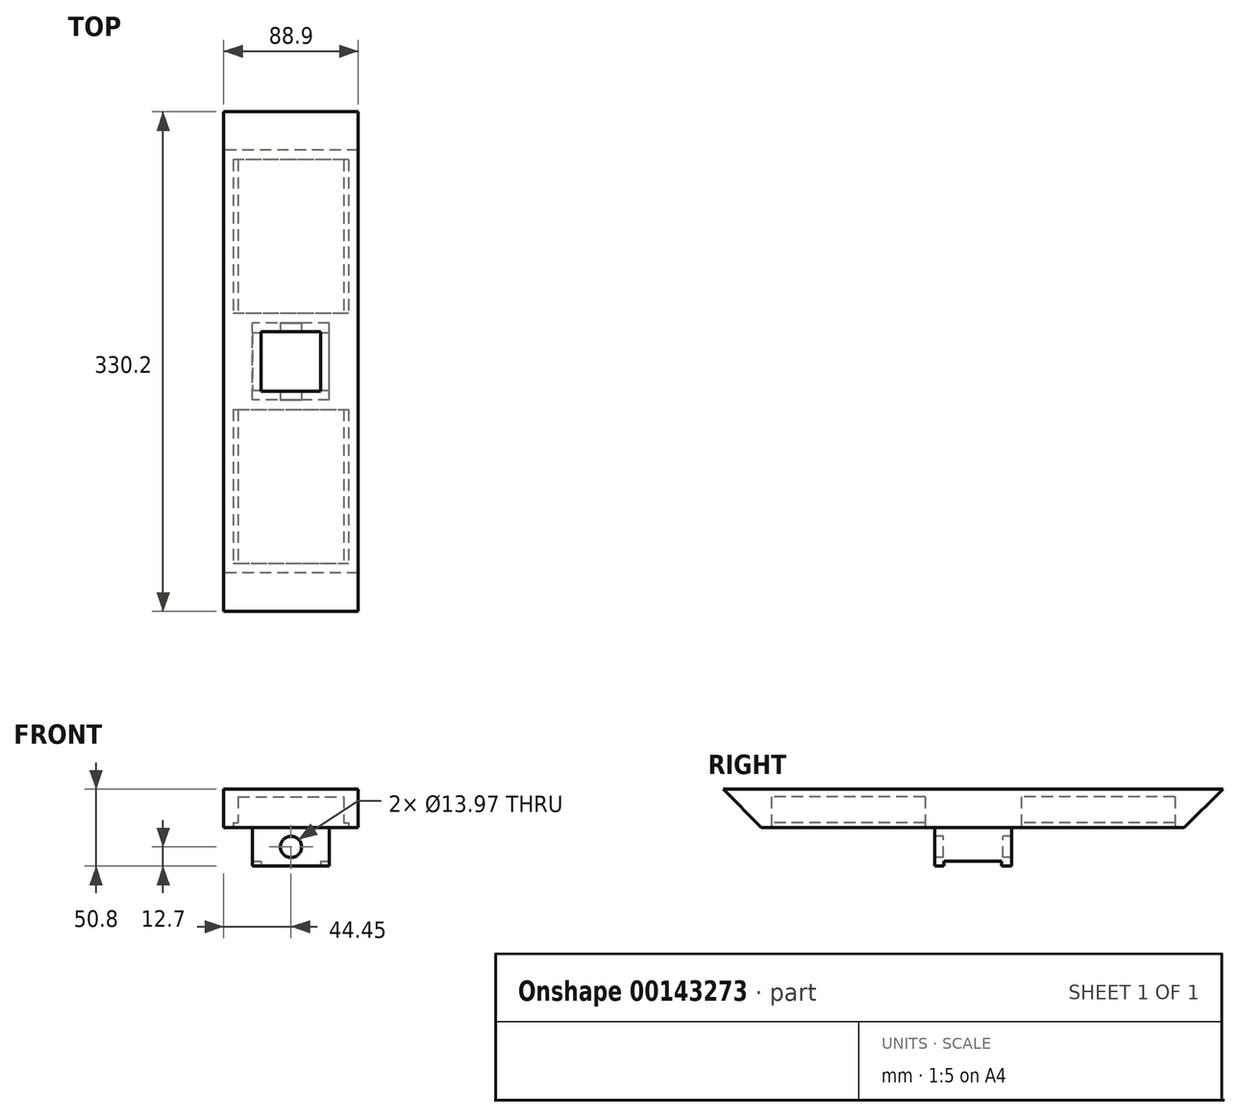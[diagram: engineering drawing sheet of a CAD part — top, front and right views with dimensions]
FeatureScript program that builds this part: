
annotation { "Feature Type Name" : "Feature", "Feature Type Description" : "" }
export const myFeature = defineFeature(function(context is Context, id is Id, definition is map)
    precondition{}
    {
        {
            var Q0;
            Q0=qCreatedBy(makeId("Top.planeOp"),FACE);
            var sketch = newSketch(context, id + "F0", { "sketchPlane" : qUnion([Q0])});
            skLineSegment(sketch, "E0.bottom", {"start": v(25.4, -25.4) * mm, "end": v(-25.4, -25.4) * mm});
            skLineSegment(sketch, "E0.top", {"start": v(25.4, 25.4) * mm, "end": v(-25.4, 25.4) * mm});
            skLineSegment(sketch, "E0.left", {"start": v(25.4, -25.4) * mm, "end": v(25.4, 25.4) * mm});
            skLineSegment(sketch, "E0.right", {"start": v(-25.4, -25.4) * mm, "end": v(-25.4, 25.4) * mm});
            skPoint(sketch, "E0.middle", {"position": v(0, 0) * mm});
            skLineSegment(sketch, "E1.bottom", {"start": v(19.69, -19.69) * mm, "end": v(-19.68, -19.69) * mm});
            skLineSegment(sketch, "E1.top", {"start": v(19.69, 19.69) * mm, "end": v(-19.69, 19.68) * mm});
            skLineSegment(sketch, "E1.left", {"start": v(19.69, -19.69) * mm, "end": v(19.69, 19.69) * mm});
            skLineSegment(sketch, "E1.right", {"start": v(-19.68, -19.69) * mm, "end": v(-19.68, 19.69) * mm});
            skSolve(sketch);
        }
        {
            var Q0;
            Q0 = qSketchRegion(id + "F0", true);
            extrude(context, id + "F1", {"entities" : qUnion([Q0]), "depth" : 25.4 * mm});
        }
        {
            var Q0;
            Q0=makeQuery(id+"F1.opExtrude","SWEPT_FACE",FACE,{"disambiguationData":[OSD([sQuery(id+"F0.wireOp",EDGE,"E0.bottom")])]});
            var sketch = newSketch(context, id + "F2", { "sketchPlane" : qUnion([Q0])});
            skCircle(sketch, "E2", {"center": v(0, 12.7) * mm, "radius": 6.99 * mm});
            skPoint(sketch, "E2.centerSnap0", {"position": v(-25.4, 12.7) * mm});
            skSolve(sketch);
        }
        {
            var Q0;
            Q0 = qSketchRegion(id + "F2", true);
            extrude(context, id + "F3", {"entities" : qUnion([Q0]), "operationType" : NewBodyOperationType.REMOVE, "endBound" : BoundingType.THROUGH_ALL, "oppositeDirection" : true, "depth" : 25.4 * mm});
        }
        {
            var Q0;
            Q0=makeQuery(id+"F1.opExtrude","CAP_FACE",FACE,{"disambiguationData":[OSD([sQuery(id+"F0.wireOp",EDGE,"E0.bottom"),sQuery(id+"F0.wireOp",EDGE,"E0.top"),sQuery(id+"F0.wireOp",EDGE,"E0.left"),sQuery(id+"F0.wireOp",EDGE,"E0.right"),sQuery(id+"F0.wireOp",EDGE,"E1.bottom"),sQuery(id+"F0.wireOp",EDGE,"E1.top"),sQuery(id+"F0.wireOp",EDGE,"E1.left"),sQuery(id+"F0.wireOp",EDGE,"E1.right")])],"isStart":false});
            var sketch = newSketch(context, id + "F4", { "sketchPlane" : qUnion([Q0])});
            skLineSegment(sketch, "E3.bottom", {"start": v(44.45, -139.7) * mm, "end": v(-44.45, -139.7) * mm});
            skLineSegment(sketch, "E3.top", {"start": v(44.45, 139.7) * mm, "end": v(-44.45, 139.7) * mm});
            skLineSegment(sketch, "E3.left", {"start": v(44.45, -139.7) * mm, "end": v(44.45, 139.7) * mm});
            skLineSegment(sketch, "E3.right", {"start": v(-44.45, -139.7) * mm, "end": v(-44.45, 139.7) * mm});
            skPoint(sketch, "E3.middle", {"position": v(0, 0) * mm});
            skLineSegment(sketch, "E4.bottom", {"start": v(19.69, 19.69) * mm, "end": v(-19.69, 19.69) * mm});
            skLineSegment(sketch, "E4.top", {"start": v(19.69, -19.69) * mm, "end": v(-19.69, -19.69) * mm});
            skLineSegment(sketch, "E4.left", {"start": v(19.69, 19.69) * mm, "end": v(19.69, -19.69) * mm});
            skLineSegment(sketch, "E4.right", {"start": v(-19.69, 19.69) * mm, "end": v(-19.69, -19.69) * mm});
            skSolve(sketch);
        }
        {
            var Q0;
            Q0 = qSketchRegion(id + "F4", true);
            extrude(context, id + "F5", {"entities" : qUnion([Q0]), "operationType" : NewBodyOperationType.ADD, "depth" : 25.4 * mm});
        }
        {
            var Q0;
            Q0=makeQuery(id+"F5.opExtrude","CAP_FACE",FACE,{"disambiguationData":[OSD([sQuery(id+"F4.wireOp",EDGE,"E3.bottom"),sQuery(id+"F4.wireOp",EDGE,"E3.top"),sQuery(id+"F4.wireOp",EDGE,"E3.left"),sQuery(id+"F4.wireOp",EDGE,"E3.right"),sQuery(id+"F4.wireOp",EDGE,"E4.bottom"),sQuery(id+"F4.wireOp",EDGE,"E4.top"),sQuery(id+"F4.wireOp",EDGE,"E4.left"),sQuery(id+"F4.wireOp",EDGE,"E4.right")])],"isStart":true});
            var sketch = newSketch(context, id + "F6", { "sketchPlane" : qUnion([Q0])});
            skLineSegment(sketch, "E5.bottom", {"start": v(44.45, 139.7) * mm, "end": v(38.1, 139.7) * mm});
            skLineSegment(sketch, "E5.top", {"start": v(44.45, 133.35) * mm, "end": v(38.1, 133.35) * mm});
            skLineSegment(sketch, "E5.left", {"start": v(44.45, 139.7) * mm, "end": v(44.45, 133.35) * mm});
            skLineSegment(sketch, "E5.right", {"start": v(38.1, 139.7) * mm, "end": v(38.1, 133.35) * mm});
            skLineSegment(sketch, "E6.bottom", {"start": v(-44.45, 25.4) * mm, "end": v(-38.1, 25.4) * mm});
            skLineSegment(sketch, "E6.top", {"start": v(-44.45, 31.75) * mm, "end": v(-38.1, 31.75) * mm});
            skLineSegment(sketch, "E6.left", {"start": v(-44.45, 25.4) * mm, "end": v(-44.45, 31.75) * mm});
            skLineSegment(sketch, "E6.right", {"start": v(-38.1, 25.4) * mm, "end": v(-38.1, 31.75) * mm});
            skLineSegment(sketch, "E7.bottom", {"start": v(-44.45, -25.4) * mm, "end": v(-38.1, -25.4) * mm});
            skLineSegment(sketch, "E7.top", {"start": v(-44.45, -31.75) * mm, "end": v(-38.1, -31.75) * mm});
            skLineSegment(sketch, "E7.left", {"start": v(-44.45, -25.4) * mm, "end": v(-44.45, -31.75) * mm});
            skLineSegment(sketch, "E7.right", {"start": v(-38.1, -25.4) * mm, "end": v(-38.1, -31.75) * mm});
            skLineSegment(sketch, "E8.bottom", {"start": v(44.45, -139.7) * mm, "end": v(38.1, -139.7) * mm});
            skLineSegment(sketch, "E8.top", {"start": v(44.45, -133.35) * mm, "end": v(38.1, -133.35) * mm});
            skLineSegment(sketch, "E8.left", {"start": v(44.45, -139.7) * mm, "end": v(44.45, -133.35) * mm});
            skLineSegment(sketch, "E8.right", {"start": v(38.1, -139.7) * mm, "end": v(38.1, -133.35) * mm});
            skLineSegment(sketch, "E9.bottom", {"start": v(38.1, -133.35) * mm, "end": v(-38.1, -133.35) * mm});
            skLineSegment(sketch, "E9.top", {"start": v(38.1, -31.75) * mm, "end": v(-38.1, -31.75) * mm});
            skLineSegment(sketch, "E9.left", {"start": v(38.1, -133.35) * mm, "end": v(38.1, -31.75) * mm});
            skLineSegment(sketch, "E9.right", {"start": v(-38.1, -133.35) * mm, "end": v(-38.1, -31.75) * mm});
            skLineSegment(sketch, "E10.bottom", {"start": v(-38.1, 31.75) * mm, "end": v(38.1, 31.75) * mm});
            skLineSegment(sketch, "E10.top", {"start": v(-38.1, 133.35) * mm, "end": v(38.1, 133.35) * mm});
            skLineSegment(sketch, "E10.left", {"start": v(-38.1, 31.75) * mm, "end": v(-38.1, 133.35) * mm});
            skLineSegment(sketch, "E10.right", {"start": v(38.1, 31.75) * mm, "end": v(38.1, 133.35) * mm});
            skSolve(sketch);
        }
        {
            var Q0;
            Q0=makeQuery(id+"F6.imprint","IMPRINT",FACE,{"disambiguationData":[TD([[makeQuery(id+"F6.imprint","IMPRINT",EDGE,{"derivedFrom":sQuery(id+"F6.wireOp",EDGE,"E9.bottom")}),-1.0]])]});
            var Q1;
            Q1=makeQuery(id+"F6.imprint","IMPRINT",FACE,{"disambiguationData":[TD([[makeQuery(id+"F6.imprint","IMPRINT",EDGE,{"derivedFrom":sQuery(id+"F6.wireOp",EDGE,"E10.bottom")}),1.0]])]});
            extrude(context, id + "F7", {"entities" : qUnion([Q0, Q1]), "operationType" : NewBodyOperationType.REMOVE, "oppositeDirection" : true, "depth" : 3.17 * mm});
        }
        {
            var Q0;
            Q0=makeQuery(id+"F7.boolean.opBoolean","COPY",FACE,{"derivedFrom":makeQuery(id+"F7.opExtrude","CAP_FACE",FACE,{"disambiguationData":[OSD([sQuery(id+"F6.wireOp",EDGE,"E9.bottom"),sQuery(id+"F6.wireOp",EDGE,"E9.top"),sQuery(id+"F6.wireOp",EDGE,"E9.left"),sQuery(id+"F6.wireOp",EDGE,"E9.right")])],"isStart":false})});
            var sketch = newSketch(context, id + "F8", { "sketchPlane" : qUnion([Q0])});
            skLineSegment(sketch, "E11", {"start": v(-38.1, -31.75) * mm, "end": v(-34.93, -31.75) * mm});
            skLineSegment(sketch, "E12", {"start": v(-34.93, -31.75) * mm, "end": v(-38.1, -31.75) * mm});
            skLineSegment(sketch, "E13", {"start": v(38.1, -133.35) * mm, "end": v(34.92, -133.35) * mm});
            skLineSegment(sketch, "E14", {"start": v(34.92, -133.35) * mm, "end": v(38.1, -133.35) * mm});
            skLineSegment(sketch, "E15.bottom", {"start": v(34.92, -133.35) * mm, "end": v(-34.92, -133.35) * mm});
            skLineSegment(sketch, "E15.top", {"start": v(34.92, -31.75) * mm, "end": v(-34.93, -31.75) * mm});
            skLineSegment(sketch, "E15.left", {"start": v(34.92, -133.35) * mm, "end": v(34.92, -31.75) * mm});
            skLineSegment(sketch, "E15.right", {"start": v(-34.93, -133.35) * mm, "end": v(-34.93, -31.75) * mm});
            skSolve(sketch);
        }
        {
            var Q0;
            Q0 = qSketchRegion(id + "F8", true);
            extrude(context, id + "F9", {"entities" : qUnion([Q0]), "operationType" : NewBodyOperationType.REMOVE, "oppositeDirection" : true, "depth" : 17.14 * mm});
        }
        {
            var Q0;
            Q0=makeQuery(id+"F7.boolean.opBoolean","COPY",FACE,{"derivedFrom":makeQuery(id+"F7.opExtrude","CAP_FACE",FACE,{"disambiguationData":[OSD([sQuery(id+"F6.wireOp",EDGE,"E10.bottom"),sQuery(id+"F6.wireOp",EDGE,"E10.top"),sQuery(id+"F6.wireOp",EDGE,"E10.left"),sQuery(id+"F6.wireOp",EDGE,"E10.right")])],"isStart":false})});
            var sketch = newSketch(context, id + "F10", { "sketchPlane" : qUnion([Q0])});
            skLineSegment(sketch, "E16", {"start": v(-38.1, 133.35) * mm, "end": v(-34.93, 133.35) * mm});
            skLineSegment(sketch, "E17", {"start": v(-34.93, 133.35) * mm, "end": v(-38.1, 133.35) * mm});
            skLineSegment(sketch, "E18", {"start": v(38.1, 31.75) * mm, "end": v(34.93, 31.75) * mm});
            skLineSegment(sketch, "E19", {"start": v(34.93, 31.75) * mm, "end": v(38.1, 31.75) * mm});
            skLineSegment(sketch, "E20.bottom", {"start": v(34.93, 31.75) * mm, "end": v(-34.93, 31.75) * mm});
            skLineSegment(sketch, "E20.top", {"start": v(34.93, 133.35) * mm, "end": v(-34.93, 133.35) * mm});
            skLineSegment(sketch, "E20.left", {"start": v(34.93, 31.75) * mm, "end": v(34.93, 133.35) * mm});
            skLineSegment(sketch, "E20.right", {"start": v(-34.93, 31.75) * mm, "end": v(-34.93, 133.35) * mm});
            skSolve(sketch);
        }
        {
            var Q0;
            Q0 = qSketchRegion(id + "F10", true);
            extrude(context, id + "F11", {"entities" : qUnion([Q0]), "operationType" : NewBodyOperationType.REMOVE, "oppositeDirection" : true, "depth" : 17.14 * mm});
        }
        {
            var Q0;
            Q0=makeQuery(id+"F1.opExtrude","SWEPT_FACE",FACE,{"disambiguationData":[OSD([sQuery(id+"F0.wireOp",EDGE,"E0.left")])]});
            var sketch = newSketch(context, id + "F12", { "sketchPlane" : qUnion([Q0])});
            skLineSegment(sketch, "E21", {"start": v(-25.4, 0) * mm, "end": v(-19.05, 0) * mm});
            skLineSegment(sketch, "E22", {"start": v(-19.05, 0) * mm, "end": v(-25.4, 0) * mm});
            skLineSegment(sketch, "E23", {"start": v(25.4, 0) * mm, "end": v(19.05, 0) * mm});
            skLineSegment(sketch, "E24", {"start": v(19.05, 0) * mm, "end": v(25.4, 0) * mm});
            skLineSegment(sketch, "E25.bottom", {"start": v(-19.05, 0) * mm, "end": v(19.05, 0) * mm});
            skLineSegment(sketch, "E25.top", {"start": v(-19.05, 3.17) * mm, "end": v(19.05, 3.17) * mm});
            skLineSegment(sketch, "E25.left", {"start": v(-19.05, 0) * mm, "end": v(-19.05, 3.17) * mm});
            skLineSegment(sketch, "E25.right", {"start": v(19.05, 0) * mm, "end": v(19.05, 3.17) * mm});
            skSolve(sketch);
        }
        {
            var Q0;
            Q0 = qSketchRegion(id + "F12", true);
            extrude(context, id + "F13", {"entities" : qUnion([Q0]), "operationType" : NewBodyOperationType.REMOVE, "endBound" : BoundingType.THROUGH_ALL, "oppositeDirection" : true, "depth" : 25.4 * mm});
        }
        {
            var Q0;
            Q0=makeQuery(id+"F5.opExtrude","SWEPT_FACE",FACE,{"disambiguationData":[OSD([sQuery(id+"F4.wireOp",EDGE,"E3.left")])]});
            var sketch = newSketch(context, id + "F14", { "sketchPlane" : qUnion([Q0])});
            skLineSegment(sketch, "E26", {"start": v(-139.7, 50.8) * mm, "end": v(-165.1, 50.8) * mm});
            skLineSegment(sketch, "E27", {"start": v(-165.1, 50.8) * mm, "end": v(-139.7, 25.4) * mm});
            skLineSegment(sketch, "E28", {"start": v(-139.7, 25.4) * mm, "end": v(-139.7, 50.8) * mm});
            skLineSegment(sketch, "E29", {"start": v(139.7, 25.4) * mm, "end": v(139.7, 50.8) * mm});
            skLineSegment(sketch, "E30", {"start": v(139.7, 50.8) * mm, "end": v(165.1, 50.8) * mm});
            skLineSegment(sketch, "E31", {"start": v(165.1, 50.8) * mm, "end": v(139.7, 25.4) * mm});
            skSolve(sketch);
        }
        {
            var Q0;
            Q0 = qSketchRegion(id + "F14", true);
            var Q1;
            Q1=makeQuery(id+"F5.opExtrude","SWEPT_FACE",FACE,{"disambiguationData":[OSD([sQuery(id+"F4.wireOp",EDGE,"E3.right")])]});
            extrude(context, id + "F15", {"entities" : qUnion([Q0]), "operationType" : NewBodyOperationType.ADD, "endBound" : BoundingType.UP_TO_SURFACE, "oppositeDirection" : true, "endBoundEntityFace" : qUnion([Q1]), "depth" : 25.4 * mm});
        }
    });
